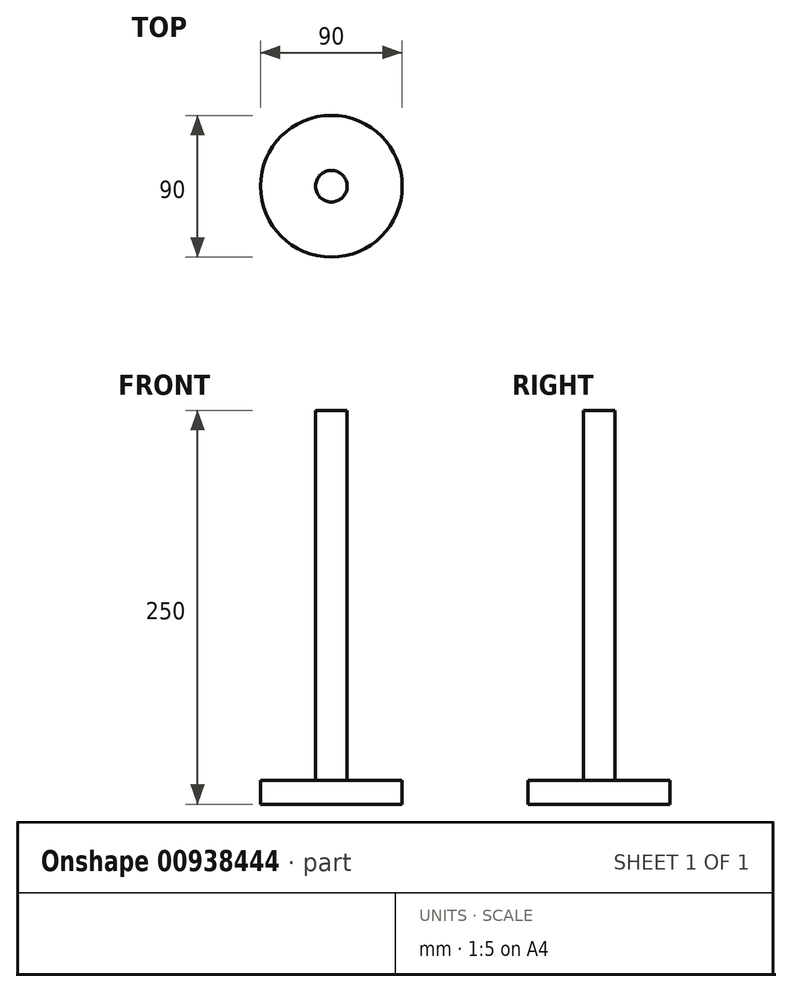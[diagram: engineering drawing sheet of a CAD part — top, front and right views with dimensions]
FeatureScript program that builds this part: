
annotation { "Feature Type Name" : "Feature", "Feature Type Description" : "" }
export const myFeature = defineFeature(function(context is Context, id is Id, definition is map)
    precondition{}
    {
        {
            var Q0;
            Q0=qCreatedBy(makeId("Front.planeOp"),FACE);
            var sketch = newSketch(context, id + "F0", { "sketchPlane" : qUnion([Q0])});
            skLineSegment(sketch, "E0", {"start": v(0, 0) * mm, "end": v(0, 250) * mm});
            skLineSegment(sketch, "E1", {"start": v(0, 250) * mm, "end": v(-10, 250) * mm});
            skLineSegment(sketch, "E2", {"start": v(-10, 250) * mm, "end": v(-10, 15) * mm});
            skLineSegment(sketch, "E3", {"start": v(-10, 15) * mm, "end": v(-45, 15) * mm});
            skLineSegment(sketch, "E4", {"start": v(-45, 15) * mm, "end": v(-45, 0) * mm});
            skLineSegment(sketch, "E5", {"start": v(-45, 0) * mm, "end": v(0, 0) * mm});
            skSolve(sketch);
        }
        {
            var Q0;
            Q0=makeQuery(id+"F0.imprint","IMPRINT",FACE,{"disambiguationData":[TD([[makeQuery(id+"F0.imprint","IMPRINT",EDGE,{"derivedFrom":sQuery(id+"F0.wireOp",EDGE,"E0")}),1.0]])]});
            var Q1;
            Q1=sQuery(id+"F0.wireOp",EDGE,"E0");
            revolve(context, id + "F1", {"surfaceOperationType" : NewSurfaceOperationType.NEW, "entities" : qUnion([Q0]), "axis" : qUnion([Q1]), "revolveType" : RevolveType.FULL});
        }
    });
